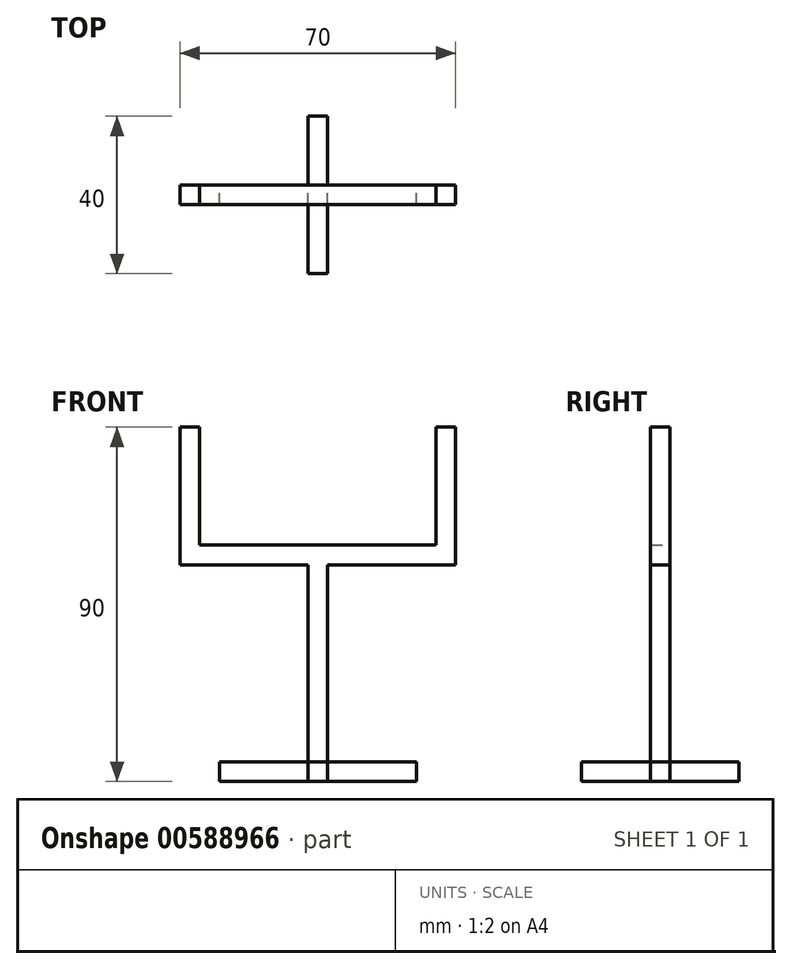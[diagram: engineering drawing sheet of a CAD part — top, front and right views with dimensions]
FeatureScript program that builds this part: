
annotation { "Feature Type Name" : "Feature", "Feature Type Description" : "" }
export const myFeature = defineFeature(function(context is Context, id is Id, definition is map)
    precondition{}
    {
        {
            var Q0;
            Q0=qCreatedBy(makeId("Front.planeOp"),FACE);
            var sketch = newSketch(context, id + "F0", { "sketchPlane" : qUnion([Q0])});
            skLineSegment(sketch, "E0.bottom", {"start": v(-2.5, 26.12) * mm, "end": v(2.5, 26.12) * mm});
            skLineSegment(sketch, "E0.top", {"start": v(-2.5, -23.88) * mm, "end": v(2.5, -23.88) * mm});
            skLineSegment(sketch, "E0.left", {"start": v(-2.5, 26.12) * mm, "end": v(-2.5, -23.88) * mm});
            skLineSegment(sketch, "E0.right", {"start": v(2.5, 26.12) * mm, "end": v(2.5, -23.88) * mm});
            skPoint(sketch, "E0.middle", {"position": v(0, 1.12) * mm});
            skLineSegment(sketch, "E1.bottom", {"start": v(-25, -23.88) * mm, "end": v(25, -23.88) * mm});
            skLineSegment(sketch, "E1.top", {"start": v(-25, -28.88) * mm, "end": v(25, -28.88) * mm});
            skLineSegment(sketch, "E1.left", {"start": v(-25, -23.88) * mm, "end": v(-25, -28.88) * mm});
            skLineSegment(sketch, "E1.right", {"start": v(25, -23.88) * mm, "end": v(25, -28.88) * mm});
            skLineSegment(sketch, "E2.bottom", {"start": v(-35, 26.12) * mm, "end": v(35, 26.12) * mm});
            skLineSegment(sketch, "E2.top", {"start": v(-35, 31.12) * mm, "end": v(35, 31.12) * mm});
            skLineSegment(sketch, "E2.left", {"start": v(-35, 26.12) * mm, "end": v(-35, 31.12) * mm});
            skLineSegment(sketch, "E2.right", {"start": v(35, 26.12) * mm, "end": v(35, 31.12) * mm});
            skLineSegment(sketch, "E3.bottom", {"start": v(35, 31.12) * mm, "end": v(30, 31.12) * mm});
            skLineSegment(sketch, "E3.top", {"start": v(35, 61.12) * mm, "end": v(30, 61.12) * mm});
            skLineSegment(sketch, "E3.left", {"start": v(35, 31.12) * mm, "end": v(35, 61.12) * mm});
            skLineSegment(sketch, "E3.right", {"start": v(30, 31.12) * mm, "end": v(30, 61.12) * mm});
            skLineSegment(sketch, "E4", {"start": v(0, 31.12) * mm, "end": v(0, 70.7) * mm, "construction": true});
            skPoint(sketch, "E4.endSnap0", {"position": v(0, 31.12) * mm});
            skLineSegment(sketch, "E5.MirrorCS", {"start": v(-30, 31.12) * mm, "end": v(-30, 61.12) * mm});
            skLineSegment(sketch, "E6.MirrorCS", {"start": v(-35, 61.12) * mm, "end": v(-30, 61.12) * mm});
            skLineSegment(sketch, "E7.MirrorCS", {"start": v(-35, 31.12) * mm, "end": v(-35, 61.12) * mm});
            skLineSegment(sketch, "E8.MirrorCS", {"start": v(-35, 31.12) * mm, "end": v(-30, 31.12) * mm});
            skSolve(sketch);
        }
        {
            var Q0;
            Q0 = qSketchRegion(id + "F0", true);
            extrude(context, id + "F1", {"entities" : qUnion([Q0]), "depth" : 5 * mm, "offsetDistance" : 25 * mm});
        }
        {
            var Q0;
            Q0=makeQuery(id+"F1.opExtrude","SWEPT_FACE",FACE,{"disambiguationData":[OSD([sQuery(id+"F0.wireOp",EDGE,"E1.top")])]});
            var sketch = newSketch(context, id + "F2", { "sketchPlane" : qUnion([Q0])});
            skLineSegment(sketch, "E9.bottom", {"start": v(-2.5, 22.5) * mm, "end": v(2.5, 22.5) * mm});
            skLineSegment(sketch, "E9.top", {"start": v(-2.5, -17.5) * mm, "end": v(2.5, -17.5) * mm});
            skLineSegment(sketch, "E9.left", {"start": v(-2.5, 22.5) * mm, "end": v(-2.5, -17.5) * mm});
            skLineSegment(sketch, "E9.right", {"start": v(2.5, 22.5) * mm, "end": v(2.5, -17.5) * mm});
            skPoint(sketch, "E9.middle", {"position": v(0, 2.5) * mm});
            skPoint(sketch, "E9.middle.positionSnap0", {"position": v(-25, 2.5) * mm});
            skPoint(sketch, "E9.centerSnap0", {"position": v(-25, 2.5) * mm});
            skSolve(sketch);
        }
        {
            var Q0;
            Q0 = qSketchRegion(id + "F2", true);
            extrude(context, id + "F3", {"entities" : qUnion([Q0]), "operationType" : NewBodyOperationType.ADD, "oppositeDirection" : true, "depth" : 5 * mm, "offsetDistance" : 25 * mm});
        }
    });
